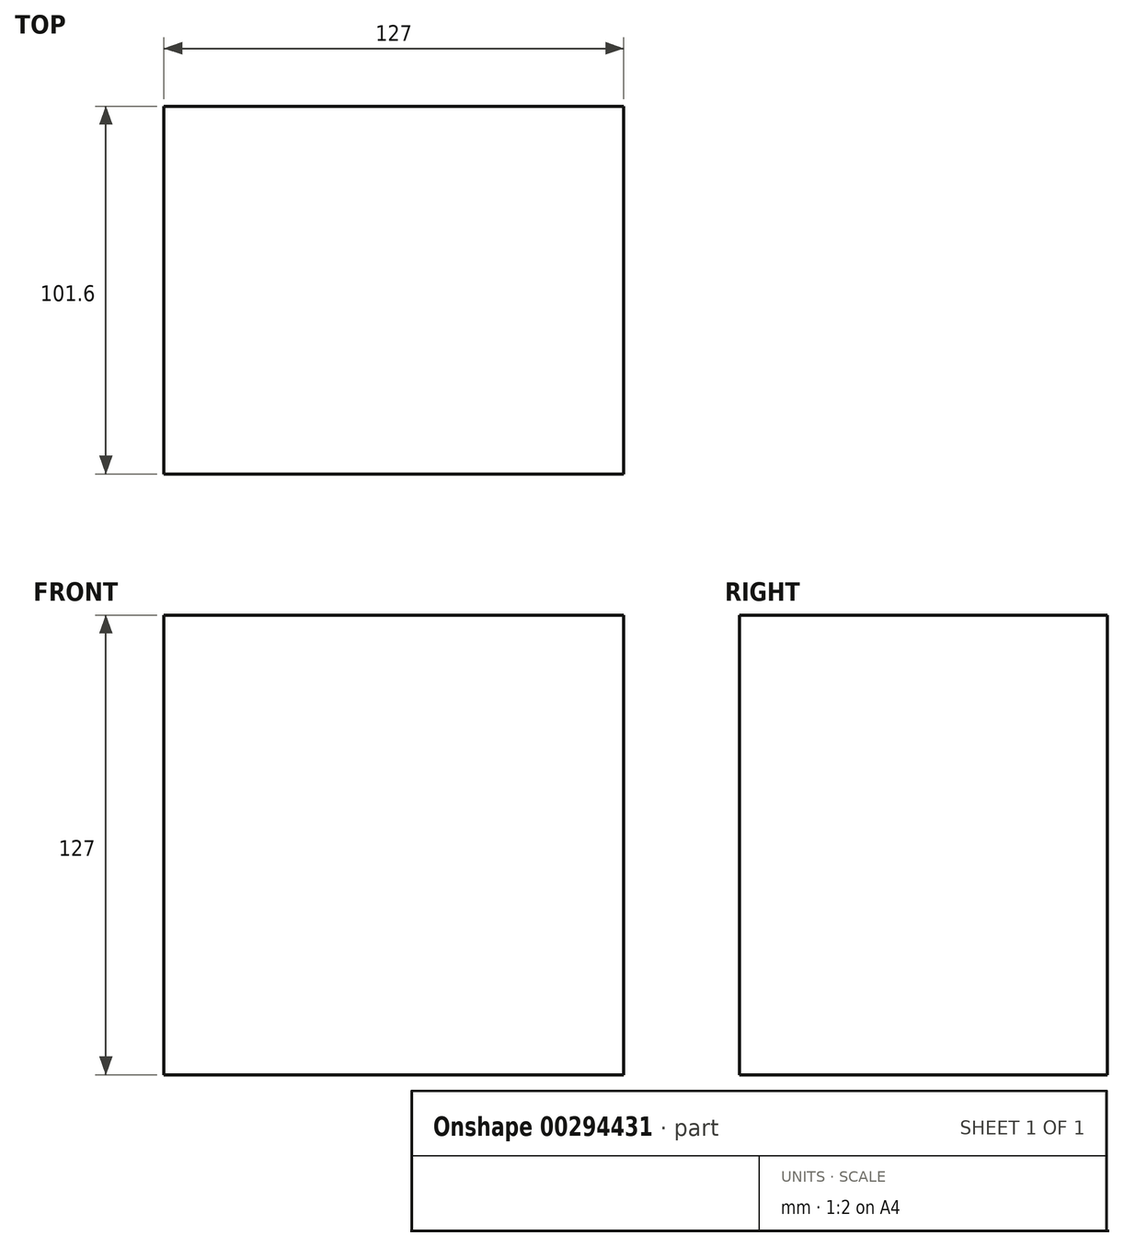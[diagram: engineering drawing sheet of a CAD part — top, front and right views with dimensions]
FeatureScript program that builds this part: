
annotation { "Feature Type Name" : "Feature", "Feature Type Description" : "" }
export const myFeature = defineFeature(function(context is Context, id is Id, definition is map)
    precondition{}
    {
        {
            var Q0;
            Q0=qCreatedBy(makeId("Top.planeOp"),FACE);
            var sketch = newSketch(context, id + "F0", { "sketchPlane" : qUnion([Q0])});
            skLineSegment(sketch, "E0.bottom", {"start": v(-52.97, 48.09) * mm, "end": v(74.03, 48.09) * mm});
            skLineSegment(sketch, "E0.top", {"start": v(-52.97, -53.51) * mm, "end": v(74.03, -53.51) * mm});
            skLineSegment(sketch, "E0.left", {"start": v(-52.97, 48.09) * mm, "end": v(-52.97, -53.51) * mm});
            skLineSegment(sketch, "E0.right", {"start": v(74.03, 48.09) * mm, "end": v(74.03, -53.51) * mm});
            skSolve(sketch);
        }
        {
            var Q0;
            Q0 = qSketchRegion(id + "F0", true);
            extrude(context, id + "F1", {"entities" : qUnion([Q0]), "depth" : 127 * mm});
        }
    });
